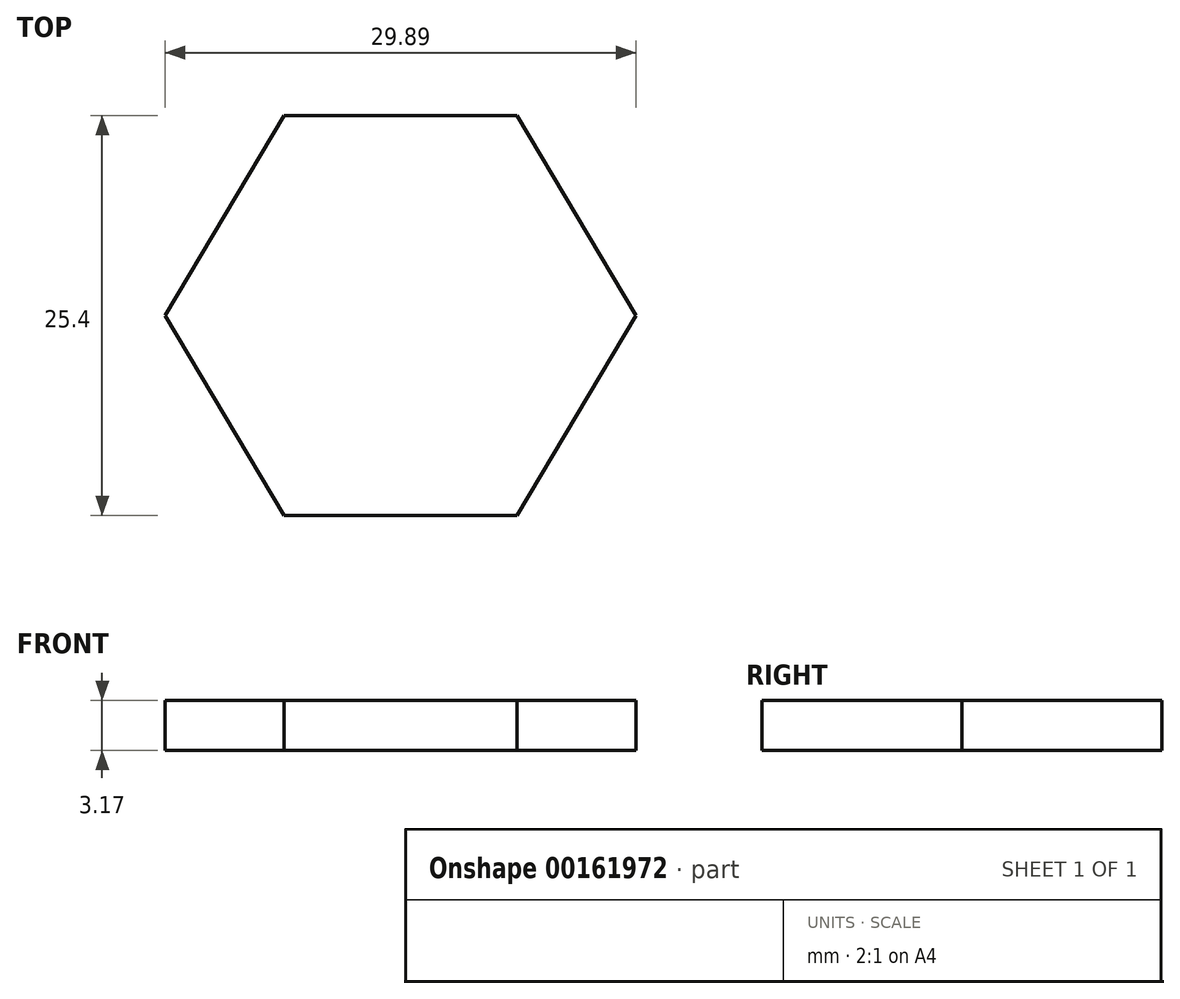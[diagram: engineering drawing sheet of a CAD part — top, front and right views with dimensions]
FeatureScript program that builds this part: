
annotation { "Feature Type Name" : "Feature", "Feature Type Description" : "" }
export const myFeature = defineFeature(function(context is Context, id is Id, definition is map)
    precondition{}
    {
        {
            var Q0;
            Q0=qCreatedBy(makeId("Top.planeOp"),FACE);
            var sketch = newSketch(context, id + "F0", { "sketchPlane" : qUnion([Q0])});
            skLineSegment(sketch, "E0", {"start": v(0, 0) * mm, "end": v(7.56, 12.7) * mm});
            skLineSegment(sketch, "E1", {"start": v(7.56, 12.7) * mm, "end": v(22.34, 12.7) * mm});
            skLineSegment(sketch, "E2", {"start": v(22.34, 12.7) * mm, "end": v(29.9, 0) * mm});
            skLineSegment(sketch, "E3", {"start": v(29.9, 0) * mm, "end": v(22.34, -12.7) * mm});
            skLineSegment(sketch, "E4", {"start": v(22.34, -12.7) * mm, "end": v(7.56, -12.7) * mm});
            skLineSegment(sketch, "E5", {"start": v(7.56, -12.7) * mm, "end": v(0, 0) * mm});
            skSolve(sketch);
        }
        {
            var Q0;
            Q0=makeQuery(id+"F0.imprint","IMPRINT",FACE,{"disambiguationData":[TD([[makeQuery(id+"F0.imprint","IMPRINT",EDGE,{"derivedFrom":sQuery(id+"F0.wireOp",EDGE,"E0")}),-1.0]])]});
            extrude(context, id + "F1", {"entities" : qUnion([Q0]), "depth" : 3.17 * mm});
        }
    });
